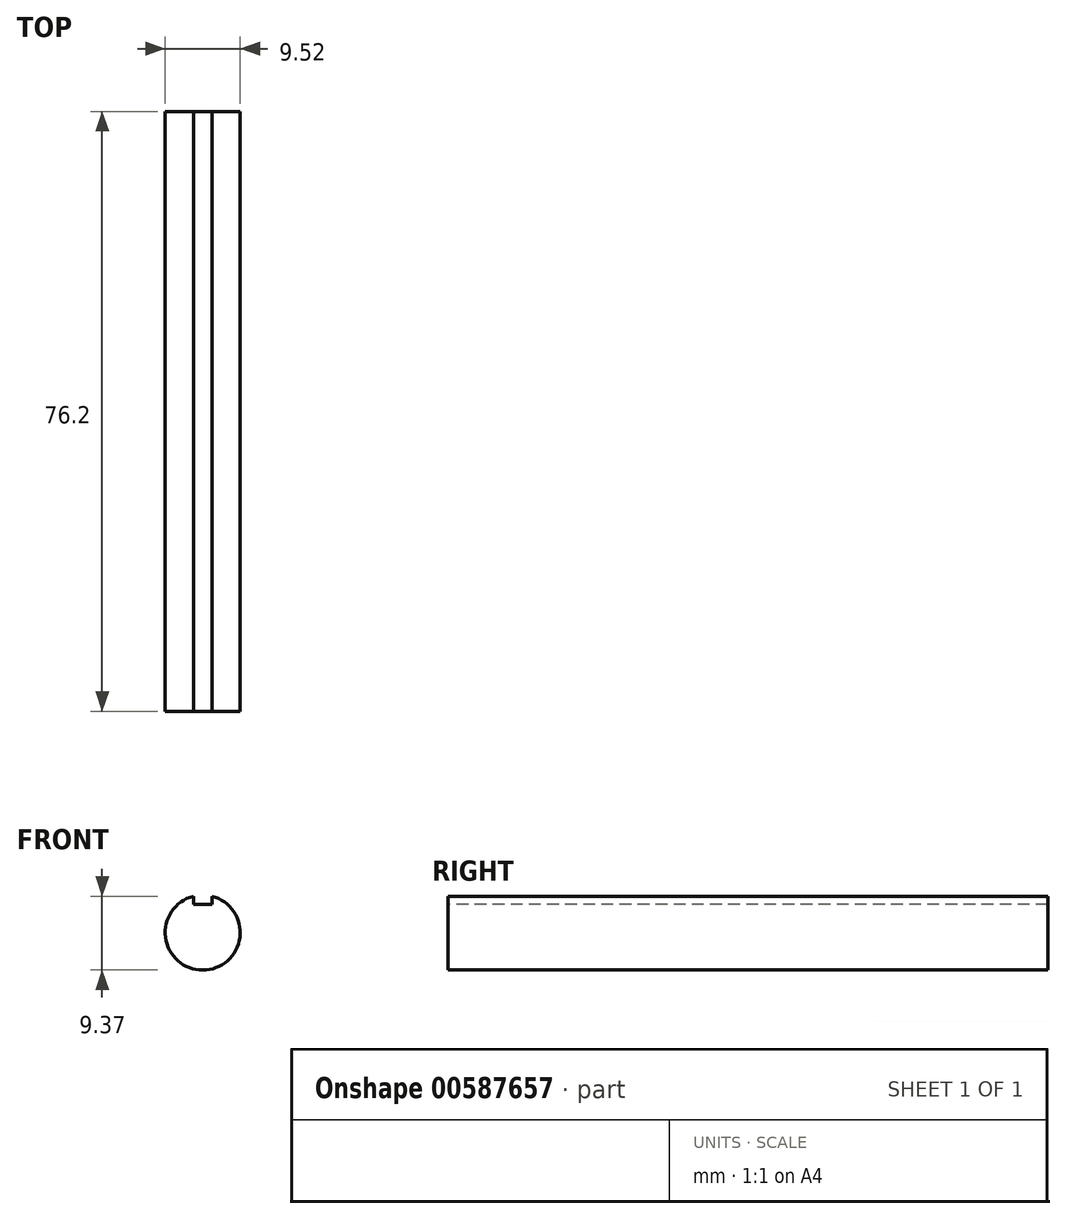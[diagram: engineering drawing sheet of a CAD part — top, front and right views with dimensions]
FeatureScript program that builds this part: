
annotation { "Feature Type Name" : "Feature", "Feature Type Description" : "" }
export const myFeature = defineFeature(function(context is Context, id is Id, definition is map)
    precondition{}
    {
        {
            var Q0;
            Q0=qCreatedBy(makeId("Front.planeOp"),FACE);
            var sketch = newSketch(context, id + "F0", { "sketchPlane" : qUnion([Q0])});
            skCircle(sketch, "E0", {"center": v(0, 0) * mm, "radius": 4.76 * mm});
            skLineSegment(sketch, "E1", {"start": v(0, 0) * mm, "end": v(0, 4.76) * mm, "construction": true});
            skLineSegment(sketch, "E2", {"start": v(-1.2, 4.61) * mm, "end": v(-1.2, 3.57) * mm});
            skLineSegment(sketch, "E3", {"start": v(1.2, 3.57) * mm, "end": v(1.2, 4.61) * mm});
            skLineSegment(sketch, "E4", {"start": v(-1.2, 3.57) * mm, "end": v(0, 3.57) * mm});
            skLineSegment(sketch, "E5", {"start": v(0, 3.57) * mm, "end": v(1.2, 3.57) * mm});
            skSolve(sketch);
        }
        {
            var Q0;
            {var subQ1=sQuery(id+"F0.wireOp",EDGE,"E2");Q0=makeQuery(id+"F0.imprint","IMPRINT",FACE,{"disambiguationData":[TD([[makeQuery(id+"F0.imprint","IMPRINT",EDGE,{"derivedFrom":subQ1}),-1.0]])]});}
            extrude(context, id + "F1", {"entities" : qUnion([Q0]), "oppositeDirection" : true, "depth" : 76.2 * mm, "offsetDistance" : 25.4 * mm});
        }
    });
